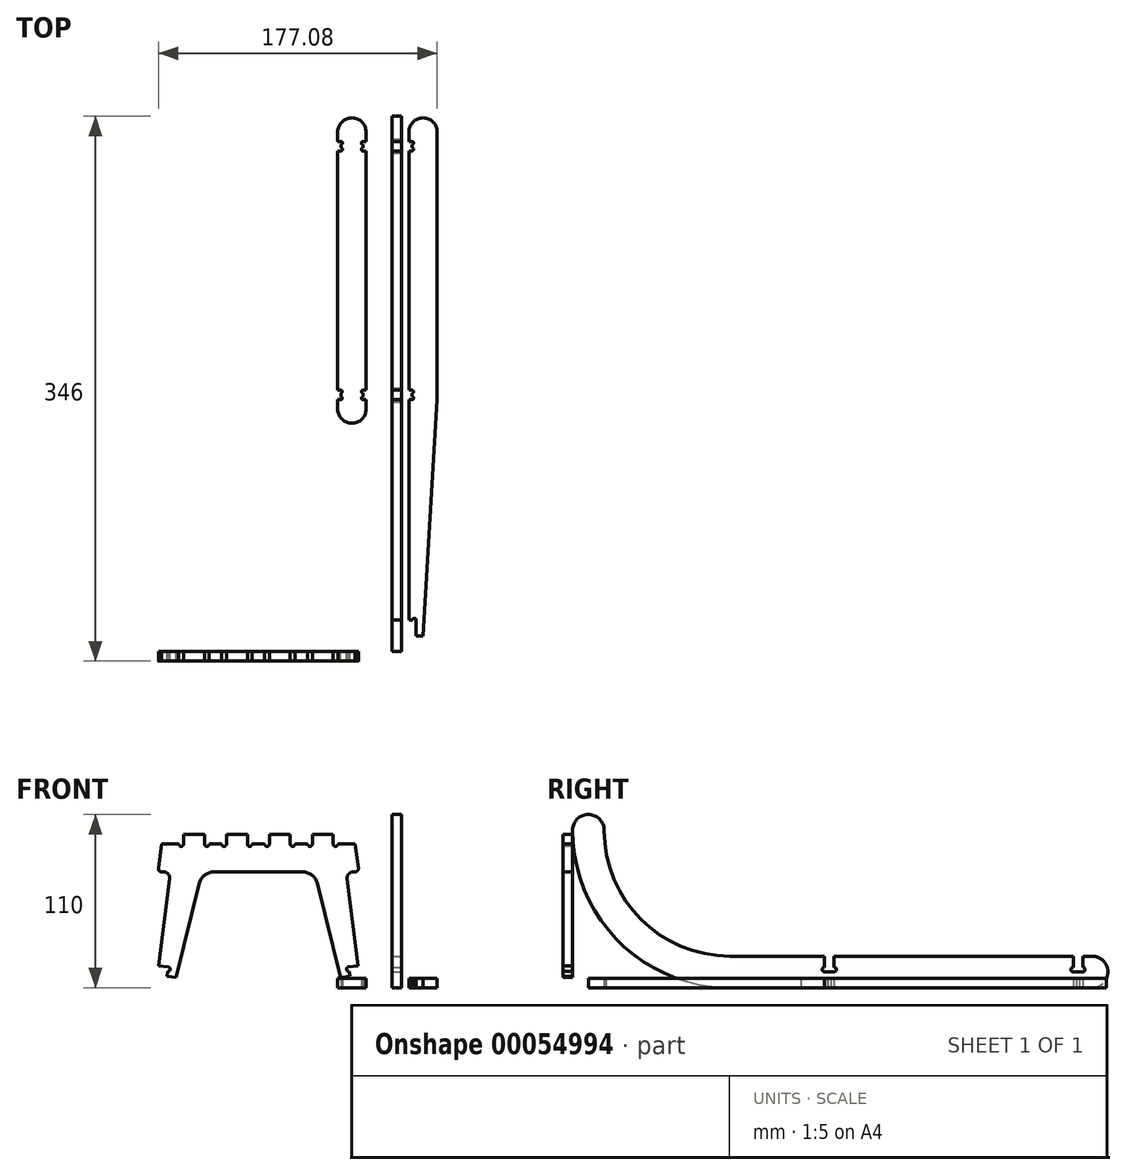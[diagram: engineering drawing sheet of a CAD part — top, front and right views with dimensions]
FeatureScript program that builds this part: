
annotation { "Feature Type Name" : "Feature", "Feature Type Description" : "" }
export const myFeature = defineFeature(function(context is Context, id is Id, definition is map)
    precondition{}
    {
        {
            var Q0;
            Q0=qCreatedBy(makeId("Right.planeOp"),FACE);
            var sketch = newSketch(context, id + "F0", { "sketchPlane" : qUnion([Q0])});
            skLineSegment(sketch, "E0", {"start": v(330, 0) * mm, "end": v(100, 0) * mm});
            skArc(sketch, "E1", {"start": v(100, 0) * mm, "mid": v(29.29, 29.29) * mm, "end": v(0, 100) * mm});
            skArc(sketch, "E2", {"start": v(0, 100) * mm, "mid": v(10, 110) * mm, "end": v(20, 100) * mm});
            skArc(sketch, "E3", {"start": v(330, 0) * mm, "mid": v(340, 10) * mm, "end": v(330, 20) * mm});
            skLineSegment(sketch, "E4", {"start": v(330, 20) * mm, "end": v(100, 20) * mm});
            skArc(sketch, "E5", {"start": v(100, 20) * mm, "mid": v(43.43, 43.43) * mm, "end": v(20, 100) * mm});
            skSolve(sketch);
        }
        {
            var Q0;
            Q0=makeQuery(id+"F0.imprint","IMPRINT",FACE,{"disambiguationData":[TD([[makeQuery(id+"F0.imprint","IMPRINT",EDGE,{"derivedFrom":sQuery(id+"F0.wireOp",EDGE,"E0")}),-1.0]])]});
            extrude(context, id + "F1", {"entities" : qUnion([Q0]), "depth" : 6 * mm});
        }
        {
            var Q0;
            Q0=qCreatedBy(makeId("Front.planeOp"),FACE);
            var sketch = newSketch(context, id + "F2", { "sketchPlane" : qUnion([Q0])});
            skLineSegment(sketch, "E6", {"start": v(-32.68, 6.5) * mm, "end": v(-47.2, 65.95) * mm});
            skLineSegment(sketch, "E7", {"start": v(-56.91, 73.58) * mm, "end": v(-84.83, 73.58) * mm});
            skLineSegment(sketch, "E8", {"start": v(-84.83, 73.58) * mm, "end": v(-84.83, 97.25) * mm, "construction": true});
            skLineSegment(sketch, "E9", {"start": v(-84.83, 97.25) * mm, "end": v(-24.06, 97.25) * mm});
            skLineSegment(sketch, "E10", {"start": v(-23.33, 73.58) * mm, "end": v(-24.52, 73.58) * mm});
            skLineSegment(sketch, "E11", {"start": v(-28.5, 69.07) * mm, "end": v(-21.53, 13.96) * mm});
            skLineSegment(sketch, "E12", {"start": v(-21.53, 13.96) * mm, "end": v(-27.48, 13.2) * mm});
            skLineSegment(sketch, "E13", {"start": v(-27.1, 10.23) * mm, "end": v(-26.73, 7.25) * mm});
            skLineSegment(sketch, "E14", {"start": v(-26.73, 7.25) * mm, "end": v(-32.68, 6.5) * mm});
            skPoint(sketch, "E15.orphan", {"position": v(-19.76, 0) * mm});
            skPoint(sketch, "E16.visualSharp", {"position": v(-49.06, 73.58) * mm});
            skArc(sketch, "E16.filletArc", {"start": v(-47.2, 65.95) * mm, "mid": v(-50.74, 71.44) * mm, "end": v(-56.91, 73.58) * mm});
            skLineSegment(sketch, "E17.MirrorCS", {"start": v(-148.12, 13.96) * mm, "end": v(-142.17, 13.2) * mm});
            skLineSegment(sketch, "E18.MirrorCS", {"start": v(-142.92, 7.25) * mm, "end": v(-136.97, 6.5) * mm});
            skArc(sketch, "E19.MirrorCS", {"start": v(-122.45, 65.95) * mm, "mid": v(-118.91, 71.44) * mm, "end": v(-112.74, 73.58) * mm});
            skLineSegment(sketch, "E20.MirrorCS", {"start": v(-146.32, 73.58) * mm, "end": v(-145.13, 73.58) * mm});
            skLineSegment(sketch, "E21.MirrorCS", {"start": v(-145.6, 97.25) * mm, "end": v(-148.3, 75.83) * mm});
            skLineSegment(sketch, "E22.MirrorCS", {"start": v(-84.83, 97.25) * mm, "end": v(-145.6, 97.25) * mm});
            skLineSegment(sketch, "E23.MirrorCS", {"start": v(-112.74, 73.58) * mm, "end": v(-84.83, 73.58) * mm});
            skLineSegment(sketch, "E24.MirrorCS", {"start": v(-136.97, 6.5) * mm, "end": v(-122.45, 65.95) * mm});
            skPoint(sketch, "E25.MirrorP", {"position": v(-149.89, 0) * mm});
            skPoint(sketch, "E26.MirrorP", {"position": v(-120.59, 73.58) * mm});
            skLineSegment(sketch, "E27.MirrorCS", {"start": v(-141.16, 69.07) * mm, "end": v(-148.12, 13.96) * mm});
            skLineSegment(sketch, "E28", {"start": v(-24.06, 97.25) * mm, "end": v(-21.35, 75.83) * mm});
            skPoint(sketch, "E29.visualSharp", {"position": v(-29.06, 73.58) * mm});
            skArc(sketch, "E29.filletArc", {"start": v(-24.52, 73.58) * mm, "mid": v(-27.53, 72.22) * mm, "end": v(-28.5, 69.07) * mm});
            skPoint(sketch, "E30.visualSharp", {"position": v(-140.59, 73.58) * mm});
            skArc(sketch, "E30.filletArc", {"start": v(-141.16, 69.07) * mm, "mid": v(-142.13, 72.22) * mm, "end": v(-145.13, 73.58) * mm});
            skArc(sketch, "E31", {"start": v(-27.48, 13.2) * mm, "mid": v(-28.78, 11.53) * mm, "end": v(-27.1, 10.23) * mm});
            skPoint(sketch, "E32.visualSharp", {"position": v(-148.59, 73.58) * mm});
            skArc(sketch, "E32.filletArc", {"start": v(-148.3, 75.83) * mm, "mid": v(-147.82, 74.25) * mm, "end": v(-146.32, 73.58) * mm});
            skPoint(sketch, "E33.visualSharp", {"position": v(-21.06, 73.58) * mm});
            skArc(sketch, "E33.filletArc", {"start": v(-23.33, 73.58) * mm, "mid": v(-21.83, 74.25) * mm, "end": v(-21.35, 75.83) * mm});
            skArc(sketch, "E34", {"start": v(-142.55, 10.23) * mm, "mid": v(-140.87, 11.53) * mm, "end": v(-142.17, 13.2) * mm});
            skLineSegment(sketch, "E35.trimOffspring", {"start": v(-142.55, 10.23) * mm, "end": v(-142.92, 7.25) * mm});
            skSolve(sketch);
        }
        {
            var Q0;
            Q0=makeQuery(id+"F2.imprint","IMPRINT",FACE,{"disambiguationData":[TD([[makeQuery(id+"F2.imprint","IMPRINT",EDGE,{"derivedFrom":sQuery(id+"F2.wireOp",EDGE,"E6")}),-1.0]])]});
            extrude(context, id + "F3", {"entities" : qUnion([Q0]), "depth" : 6 * mm});
        }
        {
            var Q0;
            Q0=makeQuery(id+"F1.opExtrude","CAP_FACE",FACE,{"disambiguationData":[OSD([sQuery(id+"F0.wireOp",EDGE,"E0"),sQuery(id+"F0.wireOp",EDGE,"E1"),sQuery(id+"F0.wireOp",EDGE,"E2"),sQuery(id+"F0.wireOp",EDGE,"E3"),sQuery(id+"F0.wireOp",EDGE,"E4"),sQuery(id+"F0.wireOp",EDGE,"E5")])],"isStart":false});
            var sketch = newSketch(context, id + "F4", { "sketchPlane" : qUnion([Q0])});
            skLineSegment(sketch, "E36.bottom", {"start": v(160, 20) * mm, "end": v(166, 20) * mm});
            skLineSegment(sketch, "E36.top", {"start": v(160, 10) * mm, "end": v(166, 10) * mm});
            skLineSegment(sketch, "E36.left", {"start": v(160, 20) * mm, "end": v(160, 13) * mm});
            skPoint(sketch, "E37.oppositeSnap0", {"position": v(340, 10) * mm});
            skLineSegment(sketch, "E37.bottom", {"start": v(324, 20) * mm, "end": v(318, 20) * mm});
            skLineSegment(sketch, "E37.top", {"start": v(324, 10) * mm, "end": v(318, 10) * mm});
            skLineSegment(sketch, "E37.left", {"start": v(324, 20) * mm, "end": v(324, 13) * mm});
            skLineSegment(sketch, "E37.right", {"start": v(318, 20) * mm, "end": v(318, 13) * mm});
            skArc(sketch, "E38", {"start": v(160, 13) * mm, "mid": v(158.5, 11.5) * mm, "end": v(160, 10) * mm});
            skLineSegment(sketch, "E39", {"start": v(166, 20) * mm, "end": v(166, 13) * mm});
            skArc(sketch, "E40", {"start": v(166, 10) * mm, "mid": v(167.5, 11.5) * mm, "end": v(166, 13) * mm});
            skArc(sketch, "E41", {"start": v(318, 13) * mm, "mid": v(316.5, 11.5) * mm, "end": v(318, 10) * mm});
            skArc(sketch, "E42", {"start": v(324, 10) * mm, "mid": v(325.5, 11.5) * mm, "end": v(324, 13) * mm});
            skSolve(sketch);
        }
        {
            var Q0;
            Q0=makeQuery(id+"F4.imprint","IMPRINT",FACE,{"disambiguationData":[TD([[makeQuery(id+"F4.imprint","IMPRINT",EDGE,{"derivedFrom":sQuery(id+"F4.wireOp",EDGE,"E36.bottom")}),1.0]])]});
            var Q1;
            Q1=makeQuery(id+"F4.imprint","IMPRINT",FACE,{"disambiguationData":[TD([[makeQuery(id+"F4.imprint","IMPRINT",EDGE,{"derivedFrom":sQuery(id+"F4.wireOp",EDGE,"E37.bottom")}),1.0]])]});
            extrude(context, id + "F5", {"entities" : qUnion([Q0, Q1]), "operationType" : NewBodyOperationType.REMOVE, "oppositeDirection" : true, "depth" : 25 * mm});
        }
        {
            var Q0;
            Q0=makeQuery(id+"F3.opExtrude","CAP_FACE",FACE,{"disambiguationData":[OSD([sQuery(id+"F2.wireOp",EDGE,"E6"),sQuery(id+"F2.wireOp",EDGE,"E7"),sQuery(id+"F2.wireOp",EDGE,"E9"),sQuery(id+"F2.wireOp",EDGE,"E10"),sQuery(id+"F2.wireOp",EDGE,"E11"),sQuery(id+"F2.wireOp",EDGE,"E12"),sQuery(id+"F2.wireOp",EDGE,"E13"),sQuery(id+"F2.wireOp",EDGE,"E14"),sQuery(id+"F2.wireOp",EDGE,"E16.filletArc"),sQuery(id+"F2.wireOp",EDGE,"E17.MirrorCS"),sQuery(id+"F2.wireOp",EDGE,"E18.MirrorCS"),sQuery(id+"F2.wireOp",EDGE,"E19.MirrorCS"),sQuery(id+"F2.wireOp",EDGE,"7753fc74-f742-4897-b0c5-886820c9fe503.MirrorCS"),sQuery(id+"F2.wireOp",EDGE,"E20.MirrorCS"),sQuery(id+"F2.wireOp",EDGE,"E21.MirrorCS"),sQuery(id+"F2.wireOp",EDGE,"E22.MirrorCS"),sQuery(id+"F2.wireOp",EDGE,"E23.MirrorCS"),sQuery(id+"F2.wireOp",EDGE,"E24.MirrorCS"),sQuery(id+"F2.wireOp",EDGE,"E27.MirrorCS"),sQuery(id+"F2.wireOp",EDGE,"E28")])],"isStart":false});
            var sketch = newSketch(context, id + "F6", { "sketchPlane" : qUnion([Q0])});
            skLineSegment(sketch, "E43.bottom", {"start": v(-64.56, 97.25) * mm, "end": v(-50.56, 97.25) * mm});
            skLineSegment(sketch, "E43.top", {"start": v(-64.56, 91.25) * mm, "end": v(-50.56, 91.25) * mm, "construction": true});
            skLineSegment(sketch, "E43.left", {"start": v(-64.56, 97.25) * mm, "end": v(-64.56, 91.25) * mm});
            skLineSegment(sketch, "E43.right", {"start": v(-50.56, 97.25) * mm, "end": v(-50.56, 91.25) * mm});
            skLineSegment(sketch, "E44.bottom", {"start": v(-37.3, 97.25) * mm, "end": v(-23.3, 97.25) * mm});
            skLineSegment(sketch, "E44.top", {"start": v(-37.3, 91.25) * mm, "end": v(-23.3, 91.25) * mm, "construction": true});
            skLineSegment(sketch, "E44.left", {"start": v(-37.3, 97.25) * mm, "end": v(-37.3, 91.25) * mm});
            skLineSegment(sketch, "E44.right", {"start": v(-23.3, 97.25) * mm, "end": v(-23.3, 91.25) * mm});
            skLineSegment(sketch, "E45.bottom", {"start": v(-91.83, 97.25) * mm, "end": v(-77.83, 97.25) * mm});
            skLineSegment(sketch, "E45.top", {"start": v(-91.83, 91.25) * mm, "end": v(-77.83, 91.25) * mm, "construction": true});
            skLineSegment(sketch, "E45.left", {"start": v(-91.83, 97.25) * mm, "end": v(-91.83, 91.25) * mm});
            skLineSegment(sketch, "E45.right", {"start": v(-77.83, 97.25) * mm, "end": v(-77.83, 91.25) * mm});
            skLineSegment(sketch, "E46.bottom", {"start": v(-119.1, 97.25) * mm, "end": v(-105.1, 97.25) * mm});
            skLineSegment(sketch, "E46.top", {"start": v(-119.1, 91.25) * mm, "end": v(-105.1, 91.25) * mm, "construction": true});
            skLineSegment(sketch, "E46.left", {"start": v(-119.1, 97.25) * mm, "end": v(-119.1, 91.25) * mm});
            skLineSegment(sketch, "E46.right", {"start": v(-105.1, 97.25) * mm, "end": v(-105.1, 91.25) * mm});
            skLineSegment(sketch, "E47.bottom", {"start": v(-132.35, 97.25) * mm, "end": v(-146.35, 97.25) * mm});
            skLineSegment(sketch, "E47.top", {"start": v(-132.35, 91.25) * mm, "end": v(-146.35, 91.25) * mm, "construction": true});
            skLineSegment(sketch, "E47.left", {"start": v(-132.35, 97.25) * mm, "end": v(-132.35, 91.25) * mm});
            skLineSegment(sketch, "E47.right", {"start": v(-146.35, 97.25) * mm, "end": v(-146.35, 91.25) * mm});
            skLineSegment(sketch, "E48", {"start": v(-132.35, 97.25) * mm, "end": v(-119.1, 97.25) * mm, "construction": true});
            skLineSegment(sketch, "E49", {"start": v(-105.1, 97.25) * mm, "end": v(-91.83, 97.25) * mm, "construction": true});
            skLineSegment(sketch, "E50", {"start": v(-77.83, 97.25) * mm, "end": v(-64.56, 97.25) * mm, "construction": true});
            skLineSegment(sketch, "E51", {"start": v(-50.56, 97.25) * mm, "end": v(-37.3, 97.25) * mm, "construction": true});
            skArc(sketch, "E52", {"start": v(-132.35, 91.25) * mm, "mid": v(-133.85, 89.75) * mm, "end": v(-135.35, 91.25) * mm});
            skLineSegment(sketch, "E53", {"start": v(-146.35, 91.25) * mm, "end": v(-135.35, 91.25) * mm});
            skArc(sketch, "E54", {"start": v(-119.1, 91.25) * mm, "mid": v(-117.6, 89.75) * mm, "end": v(-116.1, 91.25) * mm});
            skArc(sketch, "E55", {"start": v(-105.1, 91.25) * mm, "mid": v(-106.6, 89.75) * mm, "end": v(-108.1, 91.25) * mm});
            skArc(sketch, "E56", {"start": v(-91.83, 91.25) * mm, "mid": v(-90.33, 89.75) * mm, "end": v(-88.83, 91.25) * mm});
            skArc(sketch, "E57", {"start": v(-77.83, 91.25) * mm, "mid": v(-79.33, 89.75) * mm, "end": v(-80.83, 91.25) * mm});
            skArc(sketch, "E58", {"start": v(-64.56, 91.25) * mm, "mid": v(-63.06, 89.75) * mm, "end": v(-61.56, 91.25) * mm});
            skArc(sketch, "E59", {"start": v(-50.56, 91.25) * mm, "mid": v(-52.06, 89.75) * mm, "end": v(-53.56, 91.25) * mm});
            skArc(sketch, "E60", {"start": v(-37.3, 91.25) * mm, "mid": v(-35.8, 89.75) * mm, "end": v(-34.3, 91.25) * mm});
            skLineSegment(sketch, "E61", {"start": v(-23.3, 91.25) * mm, "end": v(-34.3, 91.25) * mm});
            skLineSegment(sketch, "E62", {"start": v(-53.56, 91.25) * mm, "end": v(-61.56, 91.25) * mm});
            skLineSegment(sketch, "E63", {"start": v(-80.83, 91.25) * mm, "end": v(-88.83, 91.25) * mm});
            skLineSegment(sketch, "E64", {"start": v(-108.1, 91.25) * mm, "end": v(-116.1, 91.25) * mm});
            skSolve(sketch);
        }
        {
            var Q0;
            Q0 = qSketchRegion(id + "F6", true);
            extrude(context, id + "F7", {"entities" : qUnion([Q0]), "operationType" : NewBodyOperationType.REMOVE, "oppositeDirection" : true, "depth" : 25 * mm});
        }
        {
            var Q0;
            Q0=qCreatedBy(makeId("Top.planeOp"),FACE);
            var sketch = newSketch(context, id + "F8", { "sketchPlane" : qUnion([Q0])});
            skLineSegment(sketch, "E65.left", {"start": v(-16.44, 154) * mm, "end": v(-16.44, 160) * mm});
            skLineSegment(sketch, "E65.right", {"start": v(-34.44, 154) * mm, "end": v(-34.44, 160) * mm});
            skArc(sketch, "E66", {"start": v(-34.44, 330) * mm, "mid": v(-25.44, 339) * mm, "end": v(-16.44, 330) * mm});
            skArc(sketch, "E67", {"start": v(-34.44, 154) * mm, "mid": v(-25.44, 145) * mm, "end": v(-16.44, 154) * mm});
            skLineSegment(sketch, "E68.bottom", {"start": v(-16.44, 166) * mm, "end": v(-18.44, 166) * mm});
            skLineSegment(sketch, "E68.top", {"start": v(-16.44, 160) * mm, "end": v(-18.44, 160) * mm});
            skLineSegment(sketch, "E69.bottom", {"start": v(-34.44, 166) * mm, "end": v(-32.44, 166) * mm});
            skLineSegment(sketch, "E69.top", {"start": v(-34.44, 160) * mm, "end": v(-32.44, 160) * mm});
            skLineSegment(sketch, "E70.bottom", {"start": v(-16.44, 324) * mm, "end": v(-18.44, 324) * mm});
            skLineSegment(sketch, "E70.top", {"start": v(-16.44, 318) * mm, "end": v(-18.44, 318) * mm});
            skLineSegment(sketch, "E71.bottom", {"start": v(-34.44, 324) * mm, "end": v(-32.44, 324) * mm});
            skLineSegment(sketch, "E71.top", {"start": v(-34.44, 318) * mm, "end": v(-32.44, 318) * mm});
            skLineSegment(sketch, "E72.trimOffspring", {"start": v(-16.44, 324) * mm, "end": v(-16.44, 330) * mm});
            skLineSegment(sketch, "E73.trimOffspring", {"start": v(-34.44, 324) * mm, "end": v(-34.44, 330) * mm});
            skLineSegment(sketch, "E74.trimOffspring", {"start": v(-16.44, 166) * mm, "end": v(-16.44, 318) * mm});
            skLineSegment(sketch, "E75.trimOffspring", {"start": v(-34.44, 166) * mm, "end": v(-34.44, 318) * mm});
            skArc(sketch, "E76", {"start": v(-32.44, 318) * mm, "mid": v(-31.44, 319) * mm, "end": v(-32.44, 320) * mm});
            skArc(sketch, "E77", {"start": v(-32.44, 322) * mm, "mid": v(-31.44, 323) * mm, "end": v(-32.44, 324) * mm});
            skLineSegment(sketch, "E78.trimOffspring", {"start": v(-32.44, 322) * mm, "end": v(-32.44, 320) * mm});
            skArc(sketch, "E79", {"start": v(-18.44, 320) * mm, "mid": v(-19.44, 319) * mm, "end": v(-18.44, 318) * mm});
            skArc(sketch, "E80", {"start": v(-18.44, 324) * mm, "mid": v(-19.44, 323) * mm, "end": v(-18.44, 322) * mm});
            skLineSegment(sketch, "E81.trimOffspring", {"start": v(-18.44, 322) * mm, "end": v(-18.44, 320) * mm});
            skArc(sketch, "E82", {"start": v(-32.44, 160) * mm, "mid": v(-31.53, 160.91) * mm, "end": v(-32.44, 161.83) * mm});
            skArc(sketch, "E83", {"start": v(-32.44, 164.17) * mm, "mid": v(-31.53, 165.09) * mm, "end": v(-32.44, 166) * mm});
            skLineSegment(sketch, "E84.trimOffspring", {"start": v(-32.44, 164.17) * mm, "end": v(-32.44, 161.83) * mm});
            skArc(sketch, "E85", {"start": v(-18.44, 161.83) * mm, "mid": v(-19.35, 160.91) * mm, "end": v(-18.44, 160) * mm});
            skArc(sketch, "E86", {"start": v(-18.44, 166) * mm, "mid": v(-19.35, 165.09) * mm, "end": v(-18.44, 164.17) * mm});
            skLineSegment(sketch, "E87.trimOffspring", {"start": v(-18.44, 164.17) * mm, "end": v(-18.44, 161.83) * mm});
            skSolve(sketch);
        }
        {
            var Q0;
            Q0=makeQuery(id+"F8.imprint","IMPRINT",FACE,{"disambiguationData":[TD([[makeQuery(id+"F8.imprint","IMPRINT",EDGE,{"derivedFrom":sQuery(id+"F8.wireOp",EDGE,"E65.left")}),1.0]])]});
            extrude(context, id + "F9", {"entities" : qUnion([Q0]), "depth" : 6 * mm});
        }
        {
            var Q0;
            Q0=qCreatedBy(makeId("Top.planeOp"),FACE);
            var sketch = newSketch(context, id + "F10", { "sketchPlane" : qUnion([Q0])});
            skLineSegment(sketch, "E88", {"start": v(10.76, 20) * mm, "end": v(10.76, 160) * mm});
            skArc(sketch, "E89", {"start": v(10.76, 330) * mm, "mid": v(19.76, 339) * mm, "end": v(28.76, 330) * mm});
            skLineSegment(sketch, "E90", {"start": v(28.76, 330) * mm, "end": v(28.76, 160) * mm});
            skLineSegment(sketch, "E91", {"start": v(28.76, 160) * mm, "end": v(19.76, 10) * mm});
            skLineSegment(sketch, "E92", {"start": v(19.76, 10) * mm, "end": v(15.42, 10) * mm});
            skLineSegment(sketch, "E93.bottom", {"start": v(10.76, 324) * mm, "end": v(12.76, 324) * mm});
            skLineSegment(sketch, "E93.top", {"start": v(10.76, 318) * mm, "end": v(12.76, 318) * mm});
            skLineSegment(sketch, "E94.trimOffspring", {"start": v(10.76, 324) * mm, "end": v(10.76, 330) * mm});
            skLineSegment(sketch, "E95.bottom", {"start": v(10.76, 166) * mm, "end": v(12.76, 166) * mm});
            skLineSegment(sketch, "E95.top", {"start": v(10.76, 160) * mm, "end": v(12.76, 160) * mm});
            skLineSegment(sketch, "E96.trimOffspring", {"start": v(10.76, 166) * mm, "end": v(10.76, 318) * mm});
            skLineSegment(sketch, "E97", {"start": v(10.76, 20) * mm, "end": v(13.1, 20) * mm});
            skLineSegment(sketch, "E98", {"start": v(15.42, 20) * mm, "end": v(15.42, 10) * mm});
            skArc(sketch, "E99", {"start": v(15.42, 20) * mm, "mid": v(14.25, 21.16) * mm, "end": v(13.1, 20) * mm});
            skArc(sketch, "E100", {"start": v(12.76, 160) * mm, "mid": v(13.76, 161) * mm, "end": v(12.76, 162) * mm});
            skArc(sketch, "E101", {"start": v(12.76, 164) * mm, "mid": v(13.76, 165) * mm, "end": v(12.76, 166) * mm});
            skLineSegment(sketch, "E102.trimOffspring", {"start": v(12.76, 164) * mm, "end": v(12.76, 162) * mm});
            skArc(sketch, "E103", {"start": v(12.76, 318) * mm, "mid": v(13.76, 319) * mm, "end": v(12.76, 320) * mm});
            skPoint(sketch, "E103.startSnap0", {"position": v(11.76, 318) * mm});
            skArc(sketch, "E104", {"start": v(12.76, 322) * mm, "mid": v(13.76, 323) * mm, "end": v(12.76, 324) * mm});
            skLineSegment(sketch, "E105", {"start": v(12.76, 322) * mm, "end": v(12.76, 320) * mm});
            skSolve(sketch);
        }
        {
            var Q0;
            Q0=makeQuery(id+"F10.imprint","IMPRINT",FACE,{"disambiguationData":[TD([[makeQuery(id+"F10.imprint","IMPRINT",EDGE,{"derivedFrom":sQuery(id+"F10.wireOp",EDGE,"E88")}),-1.0]])]});
            extrude(context, id + "F11", {"entities" : qUnion([Q0]), "depth" : 6 * mm});
        }
    });
